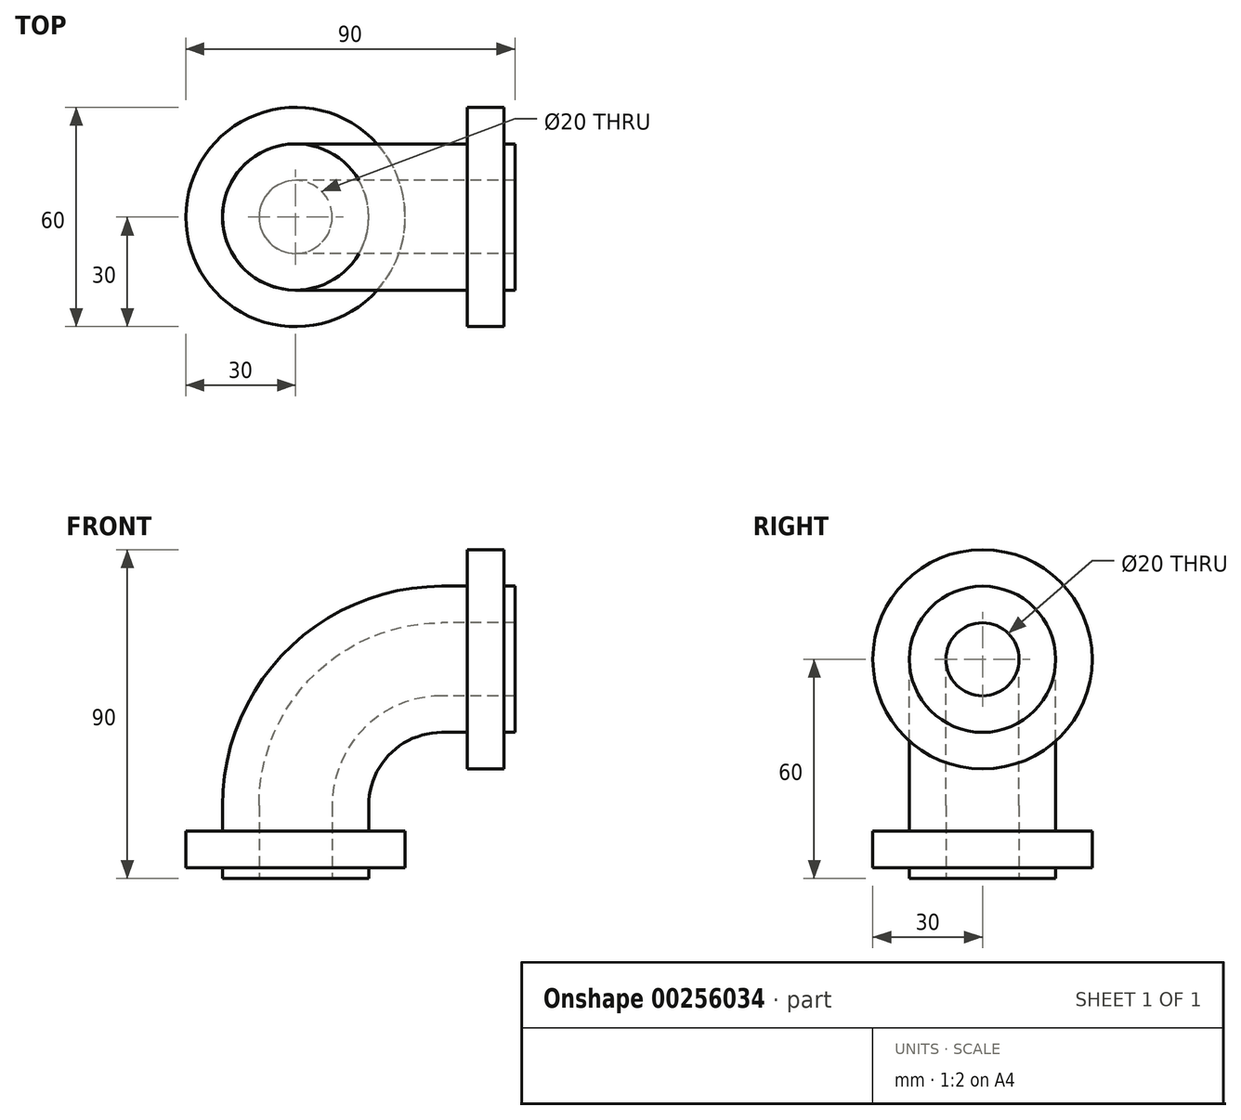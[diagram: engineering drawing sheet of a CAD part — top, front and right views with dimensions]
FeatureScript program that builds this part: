
annotation { "Feature Type Name" : "Feature", "Feature Type Description" : "" }
export const myFeature = defineFeature(function(context is Context, id is Id, definition is map)
    precondition{}
    {
        {
            var Q0;
            Q0=qCreatedBy(makeId("Right.planeOp"),FACE);
            var sketch = newSketch(context, id + "F0", { "sketchPlane" : qUnion([Q0])});
            skCircle(sketch, "E0", {"center": v(0, 0) * mm, "radius": 10 * mm});
            skCircle(sketch, "E1", {"center": v(0, 0) * mm, "radius": 20 * mm});
            skSolve(sketch);
        }
        {
            var Q0;
            Q0=qCreatedBy(makeId("Front.planeOp"),FACE);
            var sketch = newSketch(context, id + "F1", { "sketchPlane" : qUnion([Q0])});
            skLineSegment(sketch, "E2.0", {"start": v(0, 10) * mm, "end": v(0, -10) * mm});
            skLineSegment(sketch, "E3.0", {"start": v(0, 20) * mm, "end": v(0, -20) * mm});
            skLineSegment(sketch, "E4", {"start": v(0, 0) * mm, "end": v(-20, 0) * mm});
            skArc(sketch, "E5", {"start": v(-20, 0) * mm, "mid": v(-48.28, -11.72) * mm, "end": v(-60, -40) * mm});
            skLineSegment(sketch, "E6", {"start": v(-60, -40) * mm, "end": v(-60, -60) * mm});
            skSolve(sketch);
        }
        {
            var Q0;
            Q0=makeQuery(id+"F0.imprint","IMPRINT",FACE,{"disambiguationData":[TD([[makeQuery(id+"F0.imprint","IMPRINT",EDGE,{"derivedFrom":sQuery(id+"F0.wireOp",EDGE,"E0")}),-1.0]])]});
            var Q1;
            Q1=sQuery(id+"F1.wireOp",EDGE,"E4");
            var Q2;
            Q2=sQuery(id+"F1.wireOp",EDGE,"E5");
            var Q3;
            Q3=sQuery(id+"F1.wireOp",EDGE,"E6");
            sweep(context, id + "F2", {"profiles" : qUnion([Q0]), "path" : qUnion([Q1, Q2, Q3])});
        }
        {
            var Q0;
            Q0=makeQuery(id+"F2.opSweep","CAP_FACE",FACE,{"disambiguationData":[OSD([sQuery(id+"F0.wireOp",EDGE,"E0"),sQuery(id+"F0.wireOp",EDGE,"E1"),sQuery(id+"F1.wireOp",VERTEX,"E4.start")])],"isStart":true});
            cPlane(context, id + "F3", {"entities" : qUnion([Q0]), "cplaneType" : CPlaneType.OFFSET, "offset" : 3 * mm, "oppositeDirection" : true, "width" : 150 * mm, "height" : 150 * mm});
        }
        {
            var Q0;
            Q0=qCreatedBy(id+"F3.planeOp",FACE);
            var sketch = newSketch(context, id + "F4", { "sketchPlane" : qUnion([Q0])});
            skCircle(sketch, "E7", {"center": v(0, 0) * mm, "radius": 30 * mm});
            skCircle(sketch, "E8.0", {"center": v(0, 0) * mm, "radius": 20 * mm});
            skSolve(sketch);
        }
        {
            var Q0;
            Q0=makeQuery(id+"F4.imprint","IMPRINT",FACE,{"disambiguationData":[TD([[makeQuery(id+"F4.imprint","IMPRINT",EDGE,{"derivedFrom":sQuery(id+"F4.wireOp",EDGE,"E7")}),1.0]])]});
            extrude(context, id + "F5", {"entities" : qUnion([Q0]), "operationType" : NewBodyOperationType.ADD, "oppositeDirection" : true, "depth" : 10 * mm});
        }
        {
            var Q0;
            Q0=makeQuery(id+"F2.opSweep","CAP_FACE",FACE,{"disambiguationData":[OSD([sQuery(id+"F0.wireOp",EDGE,"E0"),sQuery(id+"F0.wireOp",EDGE,"E1"),sQuery(id+"F1.wireOp",VERTEX,"E6.end")])],"isStart":false});
            cPlane(context, id + "F6", {"entities" : qUnion([Q0]), "cplaneType" : CPlaneType.OFFSET, "offset" : 3 * mm, "oppositeDirection" : true, "width" : 150 * mm, "height" : 150 * mm});
        }
        {
            var Q0;
            Q0=qCreatedBy(id+"F6.planeOp",FACE);
            var sketch = newSketch(context, id + "F7", { "sketchPlane" : qUnion([Q0])});
            skCircle(sketch, "E9.0", {"center": v(-60, 0) * mm, "radius": 20 * mm});
            skCircle(sketch, "E10", {"center": v(-60, 0) * mm, "radius": 30 * mm});
            skSolve(sketch);
        }
        {
            var Q0;
            Q0=makeQuery(id+"F7.imprint","IMPRINT",FACE,{"disambiguationData":[TD([[makeQuery(id+"F7.imprint","IMPRINT",EDGE,{"derivedFrom":sQuery(id+"F7.wireOp",EDGE,"E9.0")}),-1.0]])]});
            extrude(context, id + "F8", {"entities" : qUnion([Q0]), "operationType" : NewBodyOperationType.ADD, "oppositeDirection" : true, "depth" : 10 * mm});
        }
    });
